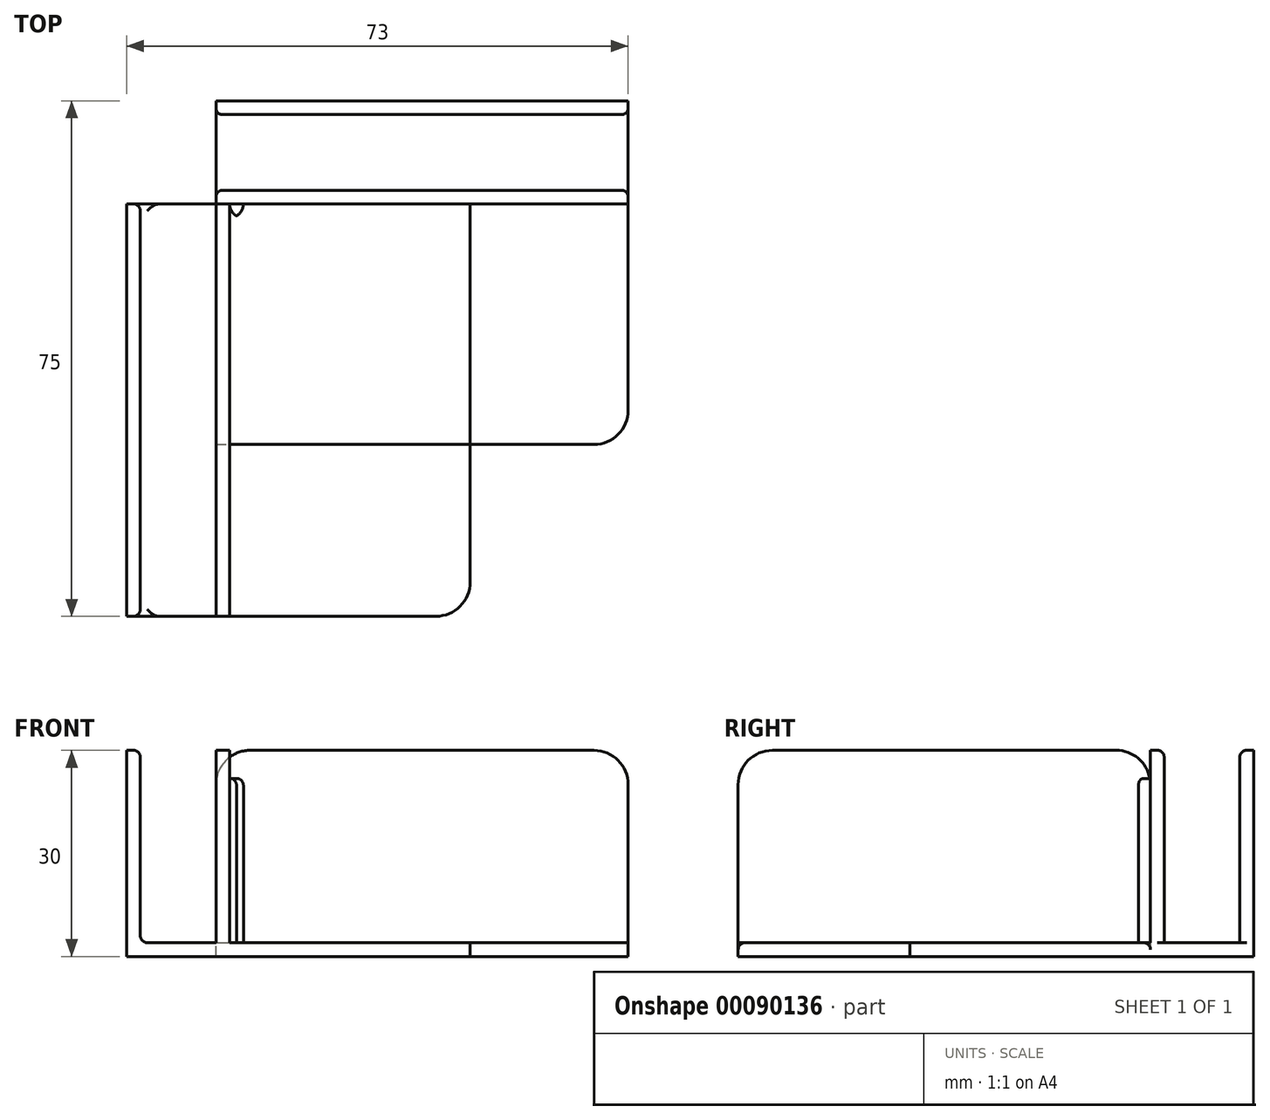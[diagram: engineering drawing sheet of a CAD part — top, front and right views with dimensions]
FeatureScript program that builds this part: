
annotation { "Feature Type Name" : "Feature", "Feature Type Description" : "" }
export const myFeature = defineFeature(function(context is Context, id is Id, definition is map)
    precondition{}
    {
        {
            var Q0;
            Q0=qCreatedBy(makeId("Front.planeOp"),FACE);
            var sketch = newSketch(context, id + "F0", { "sketchPlane" : qUnion([Q0])});
            skLineSegment(sketch, "E0.bottom", {"start": v(0, 0) * mm, "end": v(50, 0) * mm});
            skLineSegment(sketch, "E0.top", {"start": v(0, 2) * mm, "end": v(50, 2) * mm});
            skLineSegment(sketch, "E0.left", {"start": v(0, 0) * mm, "end": v(0, 2) * mm});
            skLineSegment(sketch, "E0.right", {"start": v(50, 0) * mm, "end": v(50, 2) * mm});
            skLineSegment(sketch, "E1.bottom", {"start": v(0, 0) * mm, "end": v(2, 0) * mm});
            skLineSegment(sketch, "E1.top", {"start": v(0, 30) * mm, "end": v(2, 30) * mm});
            skLineSegment(sketch, "E1.left", {"start": v(0, 0) * mm, "end": v(0, 30) * mm});
            skLineSegment(sketch, "E1.right", {"start": v(2, 0) * mm, "end": v(2, 30) * mm});
            skLineSegment(sketch, "E2.1.0.0", {"start": v(13, 0) * mm, "end": v(13, 30) * mm});
            skLineSegment(sketch, "E2.1.0.1", {"start": v(15, 0) * mm, "end": v(15, 30) * mm});
            skLineSegment(sketch, "E2.1.0.2", {"start": v(13, 0) * mm, "end": v(13, 2) * mm});
            skLineSegment(sketch, "E2.1.0.3", {"start": v(13, 0) * mm, "end": v(15, 0) * mm});
            skLineSegment(sketch, "E2.1.0.4", {"start": v(13, 30) * mm, "end": v(15, 30) * mm});
            skLineSegment(sketch, "E2.direction1", {"start": v(0, 0) * mm, "end": v(13, 0) * mm, "construction": true});
            skSolve(sketch);
        }
        {
            var Q0;
            Q0 = qSketchRegion(id + "F0", true);
            extrude(context, id + "F1", {"entities" : qUnion([Q0]), "depth" : 60 * mm});
        }
        {
            var Q0;
            Q0=makeQuery(id+"F1.opExtrude","SWEPT_BODY",BODY,{"disambiguationData":[OSD([sQuery(id+"F0.wireOp",EDGE,"E0.bottom"),sQuery(id+"F0.wireOp",EDGE,"E0.top"),sQuery(id+"F0.wireOp",EDGE,"E0.right"),sQuery(id+"F0.wireOp",EDGE,"E1.bottom"),sQuery(id+"F0.wireOp",EDGE,"E1.top"),sQuery(id+"F0.wireOp",EDGE,"E1.left"),sQuery(id+"F0.wireOp",EDGE,"E1.right"),sQuery(id+"F0.wireOp",EDGE,"E2.1.0.0"),sQuery(id+"F0.wireOp",EDGE,"E2.1.0.1"),sQuery(id+"F0.wireOp",EDGE,"E2.1.0.3"),sQuery(id+"F0.wireOp",EDGE,"E2.1.0.4")])]});
            var Q1;
            Q1=makeQuery(id+"F1.opExtrude","CAP_EDGE",EDGE,{"disambiguationData":[OSD([sQuery(id+"F0.wireOp",EDGE,"E2.1.0.1")])],"isStart":true});
            var Q2;
            Q2=makeQuery(id+"F1.opExtrude","SWEPT_EDGE",EDGE,{"disambiguationData":[OSD([sQuery(id+"F0.wireOp",EDGE,"E2.1.0.1"),sQuery(id+"F0.wireOp",EDGE,"E2.1.0.4")])]});
            transform(context, id + "F2", {"entities" : qUnion([Q0]), "transformType" : TransformType.ROTATION, "transformAxis" : qUnion([Q1]), "angle" : 90 * degree, "oppositeDirection" : true, "makeCopy" : true});
        }
        {
            var Q0;
            Q0=makeQuery(id+"F2.opPattern","COPY",BODY,{"derivedFrom":makeQuery(id+"F1.opExtrude","SWEPT_BODY",BODY,{"disambiguationData":[OSD([sQuery(id+"F0.wireOp",EDGE,"E0.bottom"),sQuery(id+"F0.wireOp",EDGE,"E0.top"),sQuery(id+"F0.wireOp",EDGE,"E0.right"),sQuery(id+"F0.wireOp",EDGE,"E1.bottom"),sQuery(id+"F0.wireOp",EDGE,"E1.top"),sQuery(id+"F0.wireOp",EDGE,"E1.left"),sQuery(id+"F0.wireOp",EDGE,"E1.right"),sQuery(id+"F0.wireOp",EDGE,"E2.1.0.0"),sQuery(id+"F0.wireOp",EDGE,"E2.1.0.1"),sQuery(id+"F0.wireOp",EDGE,"E2.1.0.3"),sQuery(id+"F0.wireOp",EDGE,"E2.1.0.4")])]}),"instanceName":"1"});
            var Q1;
            Q1=makeQuery(id+"F2.opPattern","COPY",EDGE,{"derivedFrom":makeQuery(id+"F1.opExtrude","SWEPT_EDGE",EDGE,{"disambiguationData":[OSD([sQuery(id+"F0.wireOp",EDGE,"E0.top"),sQuery(id+"F0.wireOp",EDGE,"E2.1.0.1")])]}),"instanceName":"1"});
            transform(context, id + "F3", {"entities" : qUnion([Q0]), "transformType" : TransformType.TRANSLATION_DISTANCE, "transformDirection" : qUnion([Q1]), "distance" : 58 * mm, "makeCopy" : false});
        }
        {
            var Q0;
            Q0=makeQuery(id+"F2.opPattern","COPY",EDGE,{"derivedFrom":makeQuery(id+"F1.opExtrude","CAP_EDGE",EDGE,{"disambiguationData":[OSD([sQuery(id+"F0.wireOp",EDGE,"E2.1.0.4")])],"isStart":true}),"instanceName":"1"});
            var Q1;
            Q1=makeQuery(id+"F2.opPattern","COPY",EDGE,{"derivedFrom":makeQuery(id+"F1.opExtrude","CAP_EDGE",EDGE,{"disambiguationData":[OSD([sQuery(id+"F0.wireOp",EDGE,"E1.top")])],"isStart":true}),"instanceName":"1"});
            var Q2;
            Q2=makeQuery(id+"F2.opPattern","COPY",EDGE,{"derivedFrom":makeQuery(id+"F1.opExtrude","CAP_EDGE",EDGE,{"disambiguationData":[OSD([sQuery(id+"F0.wireOp",EDGE,"E1.top")])],"isStart":false}),"instanceName":"1"});
            var Q3;
            Q3=makeQuery(id+"F2.opPattern","COPY",EDGE,{"derivedFrom":makeQuery(id+"F1.opExtrude","CAP_EDGE",EDGE,{"disambiguationData":[OSD([sQuery(id+"F0.wireOp",EDGE,"E2.1.0.4")])],"isStart":false}),"instanceName":"1"});
            var Q4;
            Q4=makeQuery(id+"F1.opExtrude","CAP_EDGE",EDGE,{"disambiguationData":[OSD([sQuery(id+"F0.wireOp",EDGE,"E2.1.0.4")])],"isStart":true});
            var Q5;
            Q5=makeQuery(id+"F1.opExtrude","CAP_EDGE",EDGE,{"disambiguationData":[OSD([sQuery(id+"F0.wireOp",EDGE,"E1.top")])],"isStart":true});
            var Q6;
            Q6=makeQuery(id+"F1.opExtrude","CAP_EDGE",EDGE,{"disambiguationData":[OSD([sQuery(id+"F0.wireOp",EDGE,"E2.1.0.4")])],"isStart":false});
            var Q7;
            Q7=makeQuery(id+"F1.opExtrude","CAP_EDGE",EDGE,{"disambiguationData":[OSD([sQuery(id+"F0.wireOp",EDGE,"E1.top")])],"isStart":false});
            var Q8;
            Q8=makeQuery(id+"F1.opExtrude","CAP_EDGE",EDGE,{"disambiguationData":[OSD([sQuery(id+"F0.wireOp",EDGE,"E0.right")])],"isStart":false});
            var Q9;
            Q9=makeQuery(id+"F2.opPattern","COPY",EDGE,{"derivedFrom":makeQuery(id+"F1.opExtrude","CAP_EDGE",EDGE,{"disambiguationData":[OSD([sQuery(id+"F0.wireOp",EDGE,"E0.right")])],"isStart":true}),"instanceName":"1"});
            var Q10;
            {var subQ0=makeQuery(id+"F1.opExtrude","SWEPT_FACE",FACE,{"disambiguationData":[OSD([sQuery(id+"F0.wireOp",EDGE,"E0.right")])]});Q10=makeQuery(id+"Fpn3AIaEYPLjJZQ_1.opBoolean","INTERSECT",EDGE,{"derivedFrom":[subQ0,makeQuery(id+"F2.opPattern","COPY",FACE,{"derivedFrom":subQ0,"instanceName":"1"})]});}
            fillet(context, id + "F4", {"entities" : qUnion([Q0, Q1, Q2, Q3, Q4, Q5, Q6, Q7, Q8, Q9, Q10]), "radius" : 5 * mm, "tangentPropagation" : true, "allowEdgeOverflow" : false});
        }
        {
            var Q0;
            {var subQ0=sQuery(id+"F0.wireOp",EDGE,"E0.top");Q0=makeQuery(id+"F2.opPattern","COPY",FACE,{"derivedFrom":makeQuery(id+"F1.opExtrude","SWEPT_FACE",FACE,{"disambiguationData":[OSD([subQ0]),TDD([makeQuery(id+"F0.imprint","IMPRINT",EDGE,{"disambiguationData":[TD([[makeQuery(id+"F0.imprint","INTERSECT",VERTEX,{"derivedFrom":[subQ0,sQuery(id+"F0.wireOp",EDGE,"E0.right")]}),1.0]])],"derivedFrom":subQ0})])]}),"instanceName":"1"});}
            var sketch = newSketch(context, id + "F5", { "sketchPlane" : qUnion([Q0])});
            skLineSegment(sketch, "E3.right", {"start": v(15, 0) * mm, "end": v(15, -2) * mm});
            skLineSegment(sketch, "E4.bottom", {"start": v(15, 0) * mm, "end": v(16.8, 0) * mm});
            skLineSegment(sketch, "E5.bottom", {"start": v(15, 0) * mm, "end": v(17, 0) * mm});
            skLineSegment(sketch, "E5.top", {"start": v(15, -2) * mm, "end": v(17, -2) * mm});
            skLineSegment(sketch, "E5.right", {"start": v(17, 0) * mm, "end": v(17, -2) * mm});
            skSolve(sketch);
        }
        {
            var Q0;
            Q0 = qSketchRegion(id + "F5", true);
            extrude(context, id + "F6", {"entities" : qUnion([Q0]), "depth" : 23.9 * mm});
        }
        {
            var Q0;
            Q0=makeQuery(id+"F6.opExtrude","SWEPT_EDGE",EDGE,{"disambiguationData":[OSD([sQuery(id+"F5.wireOp",EDGE,"E3.top"),sQuery(id+"F5.wireOp",EDGE,"E3.right")])]});
            var Q1;
            Q1=makeQuery(id+"F6.opExtrude","SWEPT_EDGE",EDGE,{"disambiguationData":[OSD([sQuery(id+"F5.wireOp",EDGE,"E5.top"),sQuery(id+"F5.wireOp",EDGE,"E5.right")])]});
            fillet(context, id + "F7", {"entities" : qUnion([Q0, Q1]), "radius" : 2 * mm, "tangentPropagation" : true, "allowEdgeOverflow" : false});
        }
        {
            var Q0;
            Q0=makeQuery(id+"F2.opPattern","COPY",EDGE,{"derivedFrom":makeQuery(id+"F1.opExtrude","CAP_EDGE",EDGE,{"disambiguationData":[OSD([sQuery(id+"F0.wireOp",EDGE,"E2.1.0.0")])],"isStart":false}),"instanceName":"1"});
            var Q1;
            {var subQ0=sQuery(id+"F5.wireOp",EDGE,"E5.right");var subQ1=sQuery(id+"F5.wireOp",EDGE,"E5.top");Q1=makeQuery(id+"F7.opFillet","BLEND_EDGE",EDGE,{"blendedFrom":[makeQuery(id+"F6.opExtrude","SWEPT_EDGE",EDGE,{"disambiguationData":[OSD([subQ1,subQ0])]}),makeQuery(id+"F6.opExtrude","CAP_FACE",FACE,{"disambiguationData":[OSD([sQuery(id+"F5.wireOp",EDGE,"E5.bottom"),subQ1,sQuery(id+"F5.wireOp",EDGE,"E3.right"),subQ0])],"isStart":false})],"blendedInto":[makeQuery(id+"F6.opExtrude","CAP_FACE",FACE,{"disambiguationData":[OSD([sQuery(id+"F5.wireOp",EDGE,"E5.bottom"),subQ1,sQuery(id+"F5.wireOp",EDGE,"E3.right"),subQ0])],"isStart":false})]});}
            var Q2;
            Q2=makeQuery(id+"F2.opPattern","COPY",EDGE,{"derivedFrom":makeQuery(id+"F1.opExtrude","SWEPT_EDGE",EDGE,{"disambiguationData":[OSD([sQuery(id+"F0.wireOp",EDGE,"E1.top"),sQuery(id+"F0.wireOp",EDGE,"E1.right")])]}),"instanceName":"1"});
            var Q3;
            Q3=makeQuery(id+"F1.opExtrude","SWEPT_FACE",FACE,{"disambiguationData":[OSD([sQuery(id+"F0.wireOp",EDGE,"E1.right")])]});
            fillet(context, id + "F8", {"entities" : qUnion([Q0, Q1, Q2, Q3]), "radius" : 1 * mm, "tangentPropagation" : true, "allowEdgeOverflow" : false});
        }
    });
